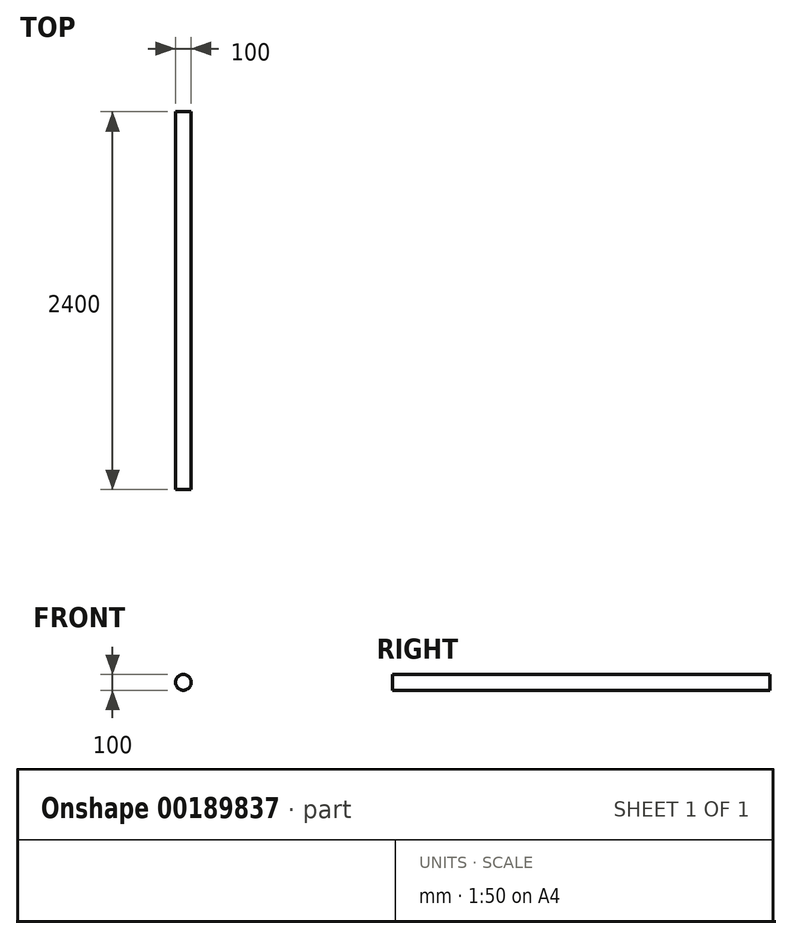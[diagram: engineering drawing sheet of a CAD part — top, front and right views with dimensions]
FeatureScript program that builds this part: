
annotation { "Feature Type Name" : "Feature", "Feature Type Description" : "" }
export const myFeature = defineFeature(function(context is Context, id is Id, definition is map)
    precondition{}
    {
        {
            var Q0;
            Q0=qCreatedBy(makeId("Front.planeOp"),FACE);
            var sketch = newSketch(context, id + "F0", { "sketchPlane" : qUnion([Q0])});
            skCircle(sketch, "E0", {"center": v(8.67, 0) * mm, "radius": 50 * mm});
            skSolve(sketch);
        }
        {
            var Q0;
            Q0=makeQuery(id+"F0.imprint","IMPRINT",FACE,{"disambiguationData":[TD([[makeQuery(id+"F0.imprint","IMPRINT",EDGE,{"derivedFrom":sQuery(id+"F0.wireOp",EDGE,"E0")}),1.0]])]});
            extrude(context, id + "F1", {"entities" : qUnion([Q0]), "depth" : 2400 * mm});
        }
    });
